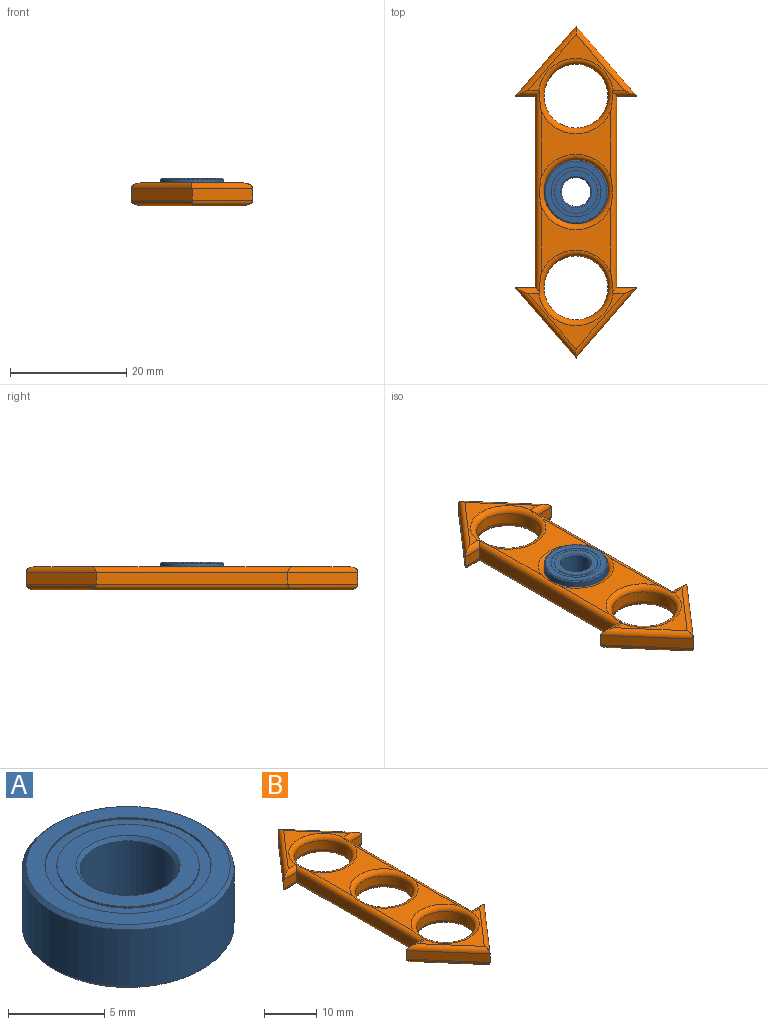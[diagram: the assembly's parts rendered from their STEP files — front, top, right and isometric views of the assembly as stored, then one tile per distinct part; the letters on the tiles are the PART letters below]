
ASSEMBLY  parts=2 mates=1
PART A: 24 faces, bbox 11x11x4 mm
  f0: plane 8.62x8.62mm, normal (0,0,1), area 15.5mm2, adj f1,f2
  f1: cylinder r=3.69mm len=7.38mm, axis (0,0,1), area 2.3mm2, adj f0,f4
  f2: cylinder r=4.31mm len=8.62mm, axis (0,0,1), area 2.7mm2, adj f0,f14
  f3: cylinder r=3.69mm len=7.38mm, axis (0,0,1), area 2.3mm2, adj f5,f15
  f4: plane 7.38x7.38mm, normal (0,0,1), area 19.9mm2, adj f1,f8
  f5: plane 7.38x7.38mm, normal (0,0,-1), area 19.9mm2, adj f3,f6
  f6: cone r=2.5mm half-angle=45deg, axis (0,0,-1), area 4.6mm2, adj f5,f7
  f7: cylinder r=2.5mm len=5mm, axis (0,0,1), area 56.5mm2, adj f6,f8
  f8: cone r=2.7mm half-angle=45deg, axis (0,0,1), area 4.6mm2, adj f4,f7
  f9: cylinder r=4.31mm len=8.62mm, axis (0,0,1), area 2.7mm2, adj f13,f15
  f10: cone r=5.5mm half-angle=45deg, axis (0,0,-1), area 9.6mm2, adj f11,f14
  f11: cylinder r=5.5mm len=11mm, axis (0,0,1), area 124.4mm2, adj f10,f12
  f12: cone r=5.3mm half-angle=45deg, axis (0,0,1), area 9.6mm2, adj f11,f13
  f13: plane 10.6x10.6mm, normal (0,0,-1), area 30mm2, adj f9,f12
  f14: plane 10.6x10.6mm, normal (0,0,1), area 30mm2, adj f2,f10
  f15: plane 8.62x8.62mm, normal (0,0,-1), area 15.5mm2, adj f3,f9
  f16: cylinder r=3.69mm len=7.38mm, axis (0,0,1), area 1.2mm2, adj f17,f19
  f17: torus R=4mm, axis (0,0,1), area 48mm2, adj f16,f18
  f18: cylinder r=3.69mm len=7.38mm, axis (0,0,1), area 1.2mm2, adj f17,f23
  f19: plane 8.62x8.62mm, normal (0,0,1), area 15.5mm2, adj f16,f20
  f20: cylinder r=4.31mm len=8.62mm, axis (0,0,1), area 1.4mm2, adj f19,f21
  f21: torus R=4mm, axis (0,0,1), area 69mm2, adj f20,f22
  f22: cylinder r=4.31mm len=8.62mm, axis (0,0,1), area 1.4mm2, adj f21,f23
  f23: plane 8.62x8.62mm, normal (0,0,-1), area 15.5mm2, adj f18,f22
PART B: 47 faces, bbox 21x57.1x4 mm
  f0: plane 16.61x9.55mm, normal (0,0,1), area 25.9mm2, adj f36,f41,f42,f45,f46
  f1: plane 16.61x9.55mm, normal (0,0,1), area 25.9mm2, adj f34,f35,f38,f39,f40
  f2: plane 12x11.5mm, normal (0,0,1), area 68.6mm2, adj f37,f39,f43,f44
  f3: plane 16.61x9.55mm, normal (0,0,-1), area 25.9mm2, adj f24,f25,f30,f31,f33
  f4: plane 16.61x9.55mm, normal (0,0,-1), area 25.9mm2, adj f21,f22,f23,f26,f27
  f5: plane 12x11.5mm, normal (0,0,-1), area 68.6mm2, adj f28,f29,f32,f33
  f6: plane 3.5x2mm, normal (0,-1,0), area 7mm2, adj f7,f17,f23,f38
  f7: plane 33x2mm, normal (-1,0,0), area 66mm2, adj f6,f8,f29,f43
  f8: plane 3.5x2mm, normal (0,1,0), area 7mm2, adj f7,f9,f30,f42
  f9: plane 12.07x10.5mm, normal (-0.75,-0.66,0), area 32mm2, adj f8,f10,f24,f36
  f10: plane 12.07x10.5mm, normal (0.75,-0.66,0), area 32mm2, adj f9,f11,f25,f41
  f11: plane 3.5x2mm, normal (0,1,0), area 7mm2, adj f10,f12,f31,f45
  f12: plane 33x2mm, normal (1,0,0), area 66mm2, adj f11,f13,f32,f44
  f13: plane 3.5x2mm, normal (0,-1,0), area 7mm2, adj f12,f14,f26,f40
  f14: plane 12.07x10.5mm, normal (0.75,0.66,0), area 32mm2, adj f13,f17,f22,f35
  f15: cylinder r=5.5mm len=11mm, axis (0,0,-1), area 69.1mm2, adj f33,f46
  f16: cylinder r=5.5mm len=11mm, axis (0,0,-1), area 69.1mm2, adj f27,f39
  f17: plane 12.07x10.5mm, normal (-0.75,0.66,0), area 32mm2, adj f6,f14,f21,f34
  f18: cylinder r=5.5mm len=11mm, axis (0,0,-1), area 69.1mm2, adj f28,f37
  f19: plane 12x11.5mm, normal (0,0,1), area 68.6mm2, adj f37,f43,f44,f46
  f20: plane 12x11.5mm, normal (0,0,-1), area 68.6mm2, adj f27,f28,f29,f32
  f21: cylinder r=1mm len=12.73mm, axis (-0.66,-0.75,0), area 23.2mm2, adj f4,f17,f22,f23
  f22: cylinder r=1mm len=12.73mm, axis (-0.66,0.75,0), area 23.2mm2, adj f4,f14,f21,f26
  f23: cylinder r=1mm len=4.27mm, axis (1,0,0), area 4.8mm2, adj f4,f6,f21,f27,f29
  f24: cylinder r=1mm len=12.73mm, axis (0.66,-0.75,0), area 23.2mm2, adj f3,f9,f25,f30
  f25: cylinder r=1mm len=12.73mm, axis (0.66,0.75,0), area 23.2mm2, adj f3,f10,f24,f31
  f26: cylinder r=1mm len=4.27mm, axis (1,0,0), area 4.8mm2, adj f4,f13,f22,f27,f32
  f27: torus R=6.5mm, axis (0,0,1), area 56.6mm2, adj f4,f16,f20,f23,f26,f29,f32
  f28: torus R=6.5mm, axis (0,0,1), area 56.2mm2, adj f5,f18,f20,f29,f32
  f29: cylinder r=1mm len=34.55mm, axis (0,-1,0), area 50.9mm2, adj f5,f7,f20,f23,f27,f28,f30,f33
  f30: cylinder r=1mm len=4.27mm, axis (-1,0,0), area 4.8mm2, adj f3,f8,f24,f29,f33
  f31: cylinder r=1mm len=4.27mm, axis (-1,0,0), area 4.8mm2, adj f3,f11,f25,f32,f33
  f32: cylinder r=1mm len=34.55mm, axis (0,1,0), area 50.9mm2, adj f5,f12,f20,f26,f27,f28,f31,f33
  f33: torus R=6.5mm, axis (0,0,1), area 56.6mm2, adj f3,f5,f15,f29,f30,f31,f32
  f34: cylinder r=1mm len=12.73mm, axis (0.66,0.75,0), area 23.2mm2, adj f1,f17,f35,f38
  f35: cylinder r=1mm len=12.73mm, axis (0.66,-0.75,0), area 23.2mm2, adj f1,f14,f34,f40
  f36: cylinder r=1mm len=12.73mm, axis (-0.66,0.75,0), area 23.2mm2, adj f0,f9,f41,f42
  f37: torus R=6.5mm, axis (0,0,1), area 56.2mm2, adj f2,f18,f19,f43,f44
  f38: cylinder r=1mm len=4.27mm, axis (-1,0,0), area 4.8mm2, adj f1,f6,f34,f39,f43
  f39: torus R=6.5mm, axis (0,0,1), area 56.6mm2, adj f1,f2,f16,f38,f40,f43,f44
  f40: cylinder r=1mm len=4.27mm, axis (-1,0,0), area 4.8mm2, adj f1,f13,f35,f39,f44
  f41: cylinder r=1mm len=12.73mm, axis (-0.66,-0.75,0), area 23.2mm2, adj f0,f10,f36,f45
  f42: cylinder r=1mm len=4.27mm, axis (1,0,0), area 4.8mm2, adj f0,f8,f36,f43,f46
  f43: cylinder r=1mm len=34.55mm, axis (0,1,0), area 50.9mm2, adj f2,f7,f19,f37,f38,f39,f42,f46
  f44: cylinder r=1mm len=34.55mm, axis (0,-1,0), area 50.9mm2, adj f2,f12,f19,f37,f39,f40,f45,f46
  f45: cylinder r=1mm len=4.27mm, axis (1,0,0), area 4.8mm2, adj f0,f11,f41,f44,f46
  f46: torus R=6.5mm, axis (0,0,1), area 56.6mm2, adj f0,f15,f19,f42,f43,f44,f45
PLACE A t=(-40.01,-2.19,7.46)mm
PLACE B t=(-40.01,-2.19,4.66)mm
MATE revolute B.f18 <-> A.f1  axis (0,0,1) through (-40.01,-2.19,5.66)mm
